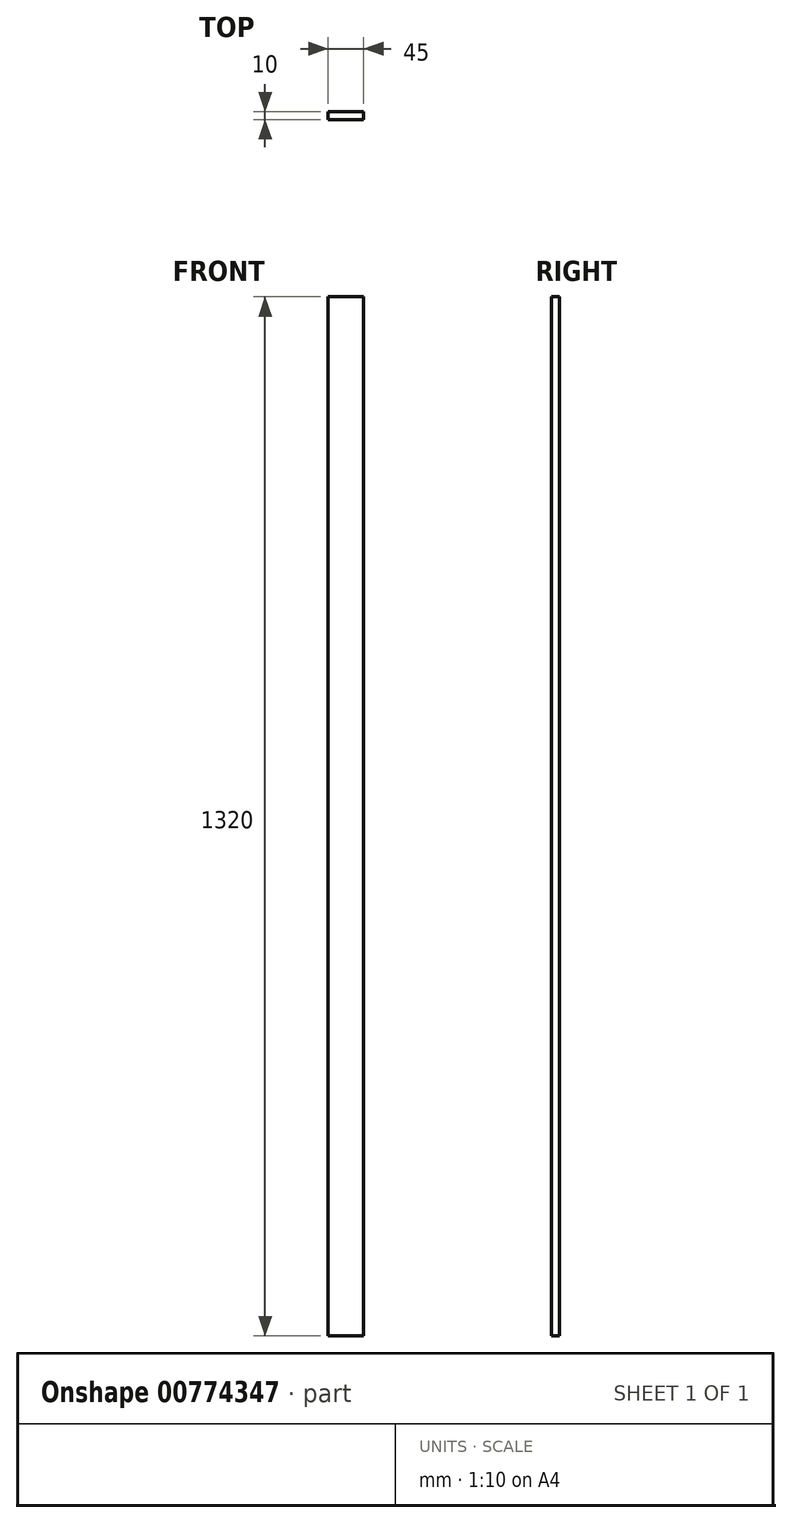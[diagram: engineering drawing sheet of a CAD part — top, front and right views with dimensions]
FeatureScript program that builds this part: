
annotation { "Feature Type Name" : "Feature", "Feature Type Description" : "" }
export const myFeature = defineFeature(function(context is Context, id is Id, definition is map)
    precondition{}
    {
        {
            var Q0;
            Q0=qCreatedBy(makeId("Top.planeOp"),FACE);
            var sketch = newSketch(context, id + "F0", { "sketchPlane" : qUnion([Q0])});
            skLineSegment(sketch, "E0.bottom", {"start": v(0, 0) * mm, "end": v(45, 0) * mm});
            skLineSegment(sketch, "E0.top", {"start": v(0, 10) * mm, "end": v(45, 10) * mm});
            skLineSegment(sketch, "E0.left", {"start": v(0, 0) * mm, "end": v(0, 10) * mm});
            skLineSegment(sketch, "E0.right", {"start": v(45, 0) * mm, "end": v(45, 10) * mm});
            skSolve(sketch);
        }
        {
            var Q0;
            Q0=makeQuery(id+"F0.imprint","IMPRINT",FACE,{"disambiguationData":[TD([[makeQuery(id+"F0.imprint","IMPRINT",EDGE,{"derivedFrom":sQuery(id+"F0.wireOp",EDGE,"E0.bottom")}),1.0]])]});
            extrude(context, id + "F1", {"entities" : qUnion([Q0]), "depth" : 1320 * mm, "offsetDistance" : 25 * mm});
        }
    });
